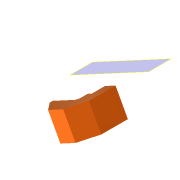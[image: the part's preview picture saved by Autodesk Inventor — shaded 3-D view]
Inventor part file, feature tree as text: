
AUTODESK INVENTOR PART (.ipt)
format: ipt  version: 2022 (Build 260153000, 153)  size: 212,992 bytes
history: native  units: in
note: dims shown in document units (in); Inventor stores cm internally (conversion verified against a paired STEP export)
features: extrude x6, other x6, sketch x5, reference x4, projected_geometry x2, plane x1
ambient origin geometry x8: Origin, YZ Plane, XZ Plane, XY Plane, X Axis, Y Axis, Z Axis, Center Point
bodies: Solid1 (feature_tree)
feature tree (24):
  plane  "Work Plane1"
  extrude  "Extrusion1"  Depth=0.5512in TaperAngle=0.0deg
  extrude  "Extrusion2"  Depth=0.0591in
  extrude  "Extrusion3"  TaperAngle=135.0deg  [1 undecoded]
  extrude  "Extrusion8"  Depth=0.2362in
  extrude  "Extrusion9"  Depth=0.5512in
  extrude  "Extrusion11"  Depth=0.3937in
  sketch  "Sketch2"  dims[d0=0.0591in d1=0.0in d3=0.5512in d4=0.0in]
  sketch  "Sketch3"  dims[d12=0.0591in d13=0.0in d22=0.5307in]
  reference  "Reference1"
  projected_geometry  "Projected Loop5"
  projected_geometry  "Projected Loop6"
  sketch  "Sketch8"  dims[d23=0.2653in d25=135.0deg]
  reference  "Reference2"
  reference  "Reference3"
  sketch  "Sketch9"  dims[d26=0.1575in d27=0.2362in]
  reference  "Reference4"
  sketch  "Skizze11"  dims[d28=0.1568in d29=0.2362in d31=0.3937in d35=0.5512in d36=0.0in d40=0.0591in d41=0.0591in d42=0.9449in d43=0.5512in d44=0.0in d45=0.0in d48=0.0in d49=0.0in]
  other  "<userpath>\Documents\Matchboxscope\INVENTOR\Matchboxscope_v0.iam"
  other  "Matchboxscope_v0.iam"
  other  "Matchboxscope_sample_v0:1"
  other  "Matchboxscope_middle2_v1:1"
  other  "00_ESP3-CAM:5"
  other  "Bauteil50"
note: 1 required parameter value undecoded (feature->parameter linkage not recoverable at this tier; creation-order binding heuristic only, values carry confidence <= 0.55)
